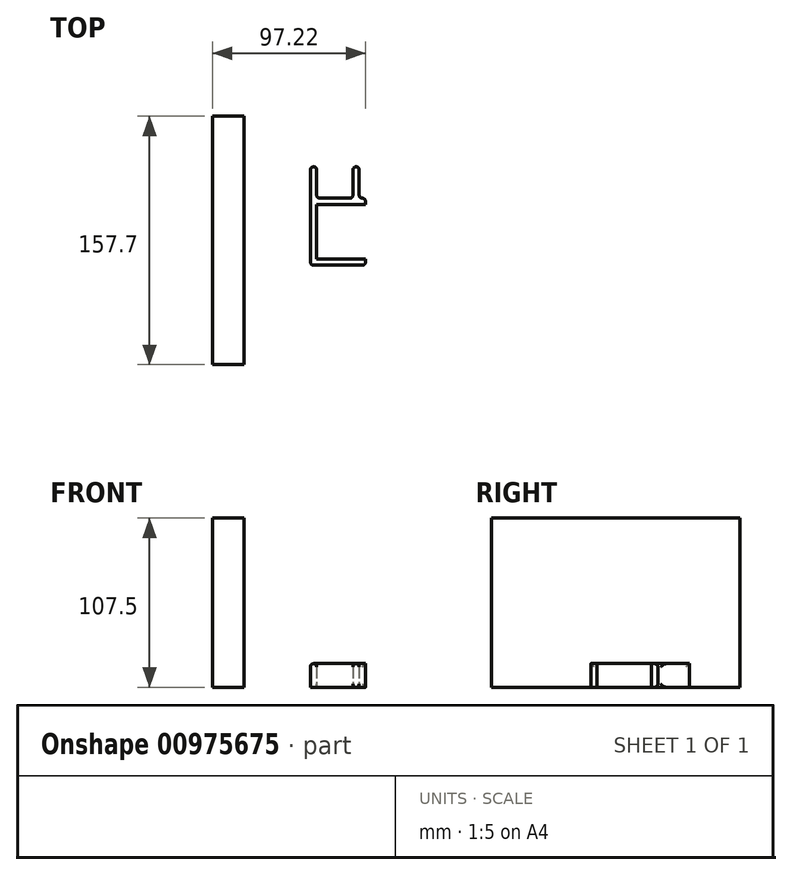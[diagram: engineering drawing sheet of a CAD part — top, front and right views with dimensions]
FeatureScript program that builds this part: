
annotation { "Feature Type Name" : "Feature", "Feature Type Description" : "" }
export const myFeature = defineFeature(function(context is Context, id is Id, definition is map)
    precondition{}
    {
        {
            var Q0;
            Q0=qCreatedBy(makeId("Top.planeOp"),FACE);
            var sketch = newSketch(context, id + "F0", { "sketchPlane" : qUnion([Q0])});
            skLineSegment(sketch, "E0", {"start": v(29.47, 14.54) * mm, "end": v(29.47, 10.54) * mm});
            skLineSegment(sketch, "E1", {"start": v(29.47, 10.54) * mm, "end": v(-1.53, 10.54) * mm});
            skLineSegment(sketch, "E2", {"start": v(-1.53, 10.54) * mm, "end": v(-1.53, -23.96) * mm});
            skLineSegment(sketch, "E3", {"start": v(-1.53, -23.96) * mm, "end": v(29.47, -23.96) * mm});
            skLineSegment(sketch, "E4", {"start": v(29.47, -23.96) * mm, "end": v(29.47, -27.96) * mm});
            skLineSegment(sketch, "E5", {"start": v(29.47, -27.96) * mm, "end": v(-5.53, -27.96) * mm});
            skLineSegment(sketch, "E6", {"start": v(-5.53, -27.96) * mm, "end": v(-5.53, 14.54) * mm});
            skLineSegment(sketch, "E7", {"start": v(-5.53, 14.54) * mm, "end": v(29.47, 14.54) * mm});
            skLineSegment(sketch, "E8.bottom", {"start": v(29.47, -23.96) * mm, "end": v(27.47, -23.96) * mm});
            skLineSegment(sketch, "E9.bottom", {"start": v(29.47, 10.54) * mm, "end": v(27.47, 10.54) * mm});
            skPoint(sketch, "E10", {"position": v(-5.53, -6.71) * mm});
            skLineSegment(sketch, "E11", {"start": v(25.47, 14.54) * mm, "end": v(25.47, 34.54) * mm});
            skLineSegment(sketch, "E12", {"start": v(21.47, 34.54) * mm, "end": v(21.47, 14.54) * mm});
            skLineSegment(sketch, "E13", {"start": v(-5.53, 14.54) * mm, "end": v(-5.53, 34.54) * mm});
            skLineSegment(sketch, "E14", {"start": v(-1.53, 34.54) * mm, "end": v(-1.53, 14.54) * mm});
            skLineSegment(sketch, "E15.bottom", {"start": v(-47.75, 66.63) * mm, "end": v(-67.75, 66.63) * mm});
            skLineSegment(sketch, "E15.top", {"start": v(-47.75, -91.07) * mm, "end": v(-67.75, -91.07) * mm});
            skLineSegment(sketch, "E15.left", {"start": v(-47.75, 66.63) * mm, "end": v(-47.75, -91.07) * mm});
            skLineSegment(sketch, "E15.right", {"start": v(-67.75, 66.63) * mm, "end": v(-67.75, -91.07) * mm});
            skLineSegment(sketch, "E16", {"start": v(-1.53, 34.54) * mm, "end": v(-5.53, 34.54) * mm});
            skLineSegment(sketch, "E17", {"start": v(21.47, 34.54) * mm, "end": v(25.47, 34.54) * mm});
            skSolve(sketch);
        }
        {
            var Q0;
            Q0=makeQuery(id+"F0.imprint","IMPRINT",FACE,{"disambiguationData":[TD([[makeQuery(id+"F0.imprint","IMPRINT",EDGE,{"derivedFrom":sQuery(id+"F0.wireOp",EDGE,"E15.bottom")}),1.0]])]});
            var Q1;
            {var subQ0=sQuery(id+"F0.wireOp",EDGE,"E11");Q1=makeQuery(id+"F0.imprint","IMPRINT",FACE,{"disambiguationData":[TD([[makeQuery(id+"F0.imprint","IMPRINT",EDGE,{"derivedFrom":subQ0}),1.0]])]});}
            var Q2;
            {var subQ5=sQuery(id+"F0.wireOp",EDGE,"E0");Q2=makeQuery(id+"F0.imprint","IMPRINT",FACE,{"disambiguationData":[TD([[makeQuery(id+"F0.imprint","IMPRINT",EDGE,{"derivedFrom":subQ5}),-1.0]])]});}
            var Q3;
            {var subQ4=sQuery(id+"F0.wireOp",EDGE,"E13");Q3=makeQuery(id+"F0.imprint","IMPRINT",FACE,{"disambiguationData":[TD([[makeQuery(id+"F0.imprint","IMPRINT",EDGE,{"derivedFrom":subQ4}),-1.0]])]});}
            extrude(context, id + "F1", {"entities" : qUnion([Q0, Q1, Q2, Q3]), "endBound" : BoundingType.SYMMETRIC, "depth" : 15 * mm, "offsetDistance" : 25 * mm});
        }
        {
            var Q0;
            {var subQ0=sQuery(id+"F0.wireOp",EDGE,"E7");Q0=makeQuery(id+"F1.opExtrude","CAP_EDGE",EDGE,{"disambiguationData":[OSD([subQ0]),TDD([makeQuery(id+"F0.imprint","IMPRINT",EDGE,{"disambiguationData":[TD([[makeQuery(id+"F0.imprint","INTERSECT",VERTEX,{"derivedFrom":[subQ0,sQuery(id+"F0.wireOp",EDGE,"E12")]}),1.0]])],"derivedFrom":subQ0})])],"isStart":false});}
            var Q1;
            {var subQ0=sQuery(id+"F0.wireOp",EDGE,"E7");Q1=makeQuery(id+"F1.opExtrude","CAP_EDGE",EDGE,{"disambiguationData":[OSD([subQ0]),TDD([makeQuery(id+"F0.imprint","IMPRINT",EDGE,{"disambiguationData":[TD([[makeQuery(id+"F0.imprint","INTERSECT",VERTEX,{"derivedFrom":[sQuery(id+"F0.wireOp",EDGE,"E0"),subQ0]}),1.0]])],"derivedFrom":subQ0})])],"isStart":false});}
            var Q2;
            {var subQ0=sQuery(id+"F0.wireOp",EDGE,"E7");Q2=makeQuery(id+"F1.opExtrude","CAP_EDGE",EDGE,{"disambiguationData":[OSD([subQ0]),TDD([makeQuery(id+"F0.imprint","IMPRINT",EDGE,{"disambiguationData":[TD([[makeQuery(id+"F0.imprint","INTERSECT",VERTEX,{"derivedFrom":[subQ0,sQuery(id+"F0.wireOp",EDGE,"E12")]}),1.0]])],"derivedFrom":subQ0})])],"isStart":true});}
            var Q3;
            {var subQ0=sQuery(id+"F0.wireOp",EDGE,"E7");Q3=makeQuery(id+"F1.opExtrude","CAP_EDGE",EDGE,{"disambiguationData":[OSD([subQ0]),TDD([makeQuery(id+"F0.imprint","IMPRINT",EDGE,{"disambiguationData":[TD([[makeQuery(id+"F0.imprint","INTERSECT",VERTEX,{"derivedFrom":[sQuery(id+"F0.wireOp",EDGE,"E0"),subQ0]}),1.0]])],"derivedFrom":subQ0})])],"isStart":true});}
            var Q4;
            Q4=makeQuery(id+"F1.opExtrude","CAP_EDGE",EDGE,{"disambiguationData":[OSD([sQuery(id+"F0.wireOp",EDGE,"E6"),sQuery(id+"F0.wireOp",EDGE,"E13")])],"isStart":false});
            var Q5;
            Q5=makeQuery(id+"F1.opExtrude","SWEPT_EDGE",EDGE,{"disambiguationData":[OSD([sQuery(id+"F0.wireOp",EDGE,"E4"),sQuery(id+"F0.wireOp",EDGE,"E5")])]});
            var Q6;
            Q6=makeQuery(id+"F1.opExtrude","SWEPT_EDGE",EDGE,{"disambiguationData":[OSD([sQuery(id+"F0.wireOp",EDGE,"E5"),sQuery(id+"F0.wireOp",EDGE,"E6")])]});
            var Q7;
            Q7=makeQuery(id+"F1.opExtrude","SWEPT_EDGE",EDGE,{"disambiguationData":[OSD([sQuery(id+"F0.wireOp",EDGE,"E0"),sQuery(id+"F0.wireOp",EDGE,"E7")])]});
            var Q8;
            Q8=makeQuery(id+"F1.opExtrude","SWEPT_EDGE",EDGE,{"disambiguationData":[OSD([sQuery(id+"F0.wireOp",EDGE,"E11"),sQuery(id+"F0.wireOp",EDGE,"E17")])]});
            var Q9;
            Q9=makeQuery(id+"F1.opExtrude","SWEPT_EDGE",EDGE,{"disambiguationData":[OSD([sQuery(id+"F0.wireOp",EDGE,"E14"),sQuery(id+"F0.wireOp",EDGE,"E16")])]});
            var Q10;
            Q10=makeQuery(id+"F1.opExtrude","SWEPT_EDGE",EDGE,{"disambiguationData":[OSD([sQuery(id+"F0.wireOp",EDGE,"E12"),sQuery(id+"F0.wireOp",EDGE,"E17")])]});
            var Q11;
            Q11=makeQuery(id+"F1.opExtrude","SWEPT_EDGE",EDGE,{"disambiguationData":[OSD([sQuery(id+"F0.wireOp",EDGE,"E13"),sQuery(id+"F0.wireOp",EDGE,"E16")])]});
            var Q12;
            Q12=makeQuery(id+"F1.opExtrude","SWEPT_EDGE",EDGE,{"disambiguationData":[OSD([sQuery(id+"F0.wireOp",EDGE,"E7"),sQuery(id+"F0.wireOp",EDGE,"E11")])]});
            var Q13;
            Q13=makeQuery(id+"F1.opExtrude","SWEPT_EDGE",EDGE,{"disambiguationData":[OSD([sQuery(id+"F0.wireOp",EDGE,"E7"),sQuery(id+"F0.wireOp",EDGE,"E12")])]});
            var Q14;
            Q14=makeQuery(id+"F1.opExtrude","SWEPT_EDGE",EDGE,{"disambiguationData":[OSD([sQuery(id+"F0.wireOp",EDGE,"E7"),sQuery(id+"F0.wireOp",EDGE,"E14")])]});
            fillet(context, id + "F2", {"entities" : qUnion([Q0, Q1, Q2, Q3, Q4, Q5, Q6, Q7, Q8, Q9, Q10, Q11, Q12, Q13, Q14]), "radius" : 2 * mm, "tangentPropagation" : true, "defaultsChanged" : false, "vertexSettings" : [], "allowEdgeOverflow" : false});
        }
        {
            var Q0;
            Q0=makeQuery(id+"F0.imprint","IMPRINT",FACE,{"disambiguationData":[TD([[makeQuery(id+"F0.imprint","IMPRINT",EDGE,{"derivedFrom":sQuery(id+"F0.wireOp",EDGE,"E15.bottom")}),1.0]])]});
            extrude(context, id + "F3", {"entities" : qUnion([Q0]), "operationType" : NewBodyOperationType.ADD, "depth" : 100 * mm, "offsetDistance" : 25 * mm});
        }
    });
